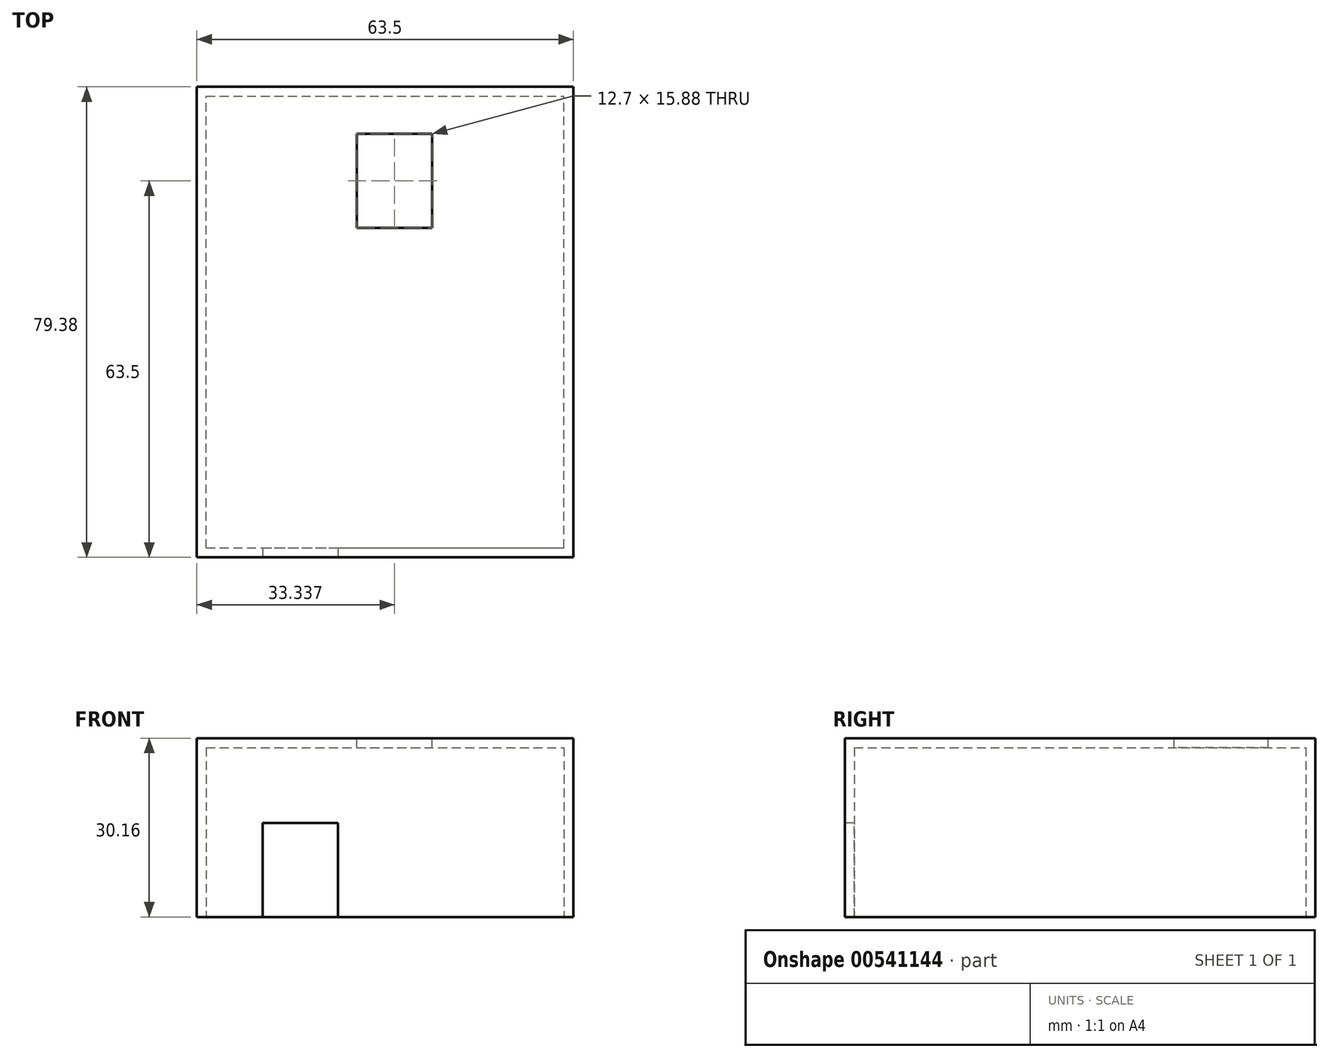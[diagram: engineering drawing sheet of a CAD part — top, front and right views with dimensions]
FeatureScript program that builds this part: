
annotation { "Feature Type Name" : "Feature", "Feature Type Description" : "" }
export const myFeature = defineFeature(function(context is Context, id is Id, definition is map)
    precondition{}
    {
        {
            var Q0;
            Q0=qCreatedBy(makeId("Top.planeOp"),FACE);
            var sketch = newSketch(context, id + "F0", { "sketchPlane" : qUnion([Q0])});
            skLineSegment(sketch, "E0.bottom", {"start": v(0, 0) * mm, "end": v(63.5, 0) * mm});
            skLineSegment(sketch, "E0.top", {"start": v(0, 79.38) * mm, "end": v(63.5, 79.38) * mm});
            skLineSegment(sketch, "E0.left", {"start": v(0, 0) * mm, "end": v(0, 79.38) * mm});
            skLineSegment(sketch, "E0.right", {"start": v(63.5, 0) * mm, "end": v(63.5, 79.38) * mm});
            skLineSegment(sketch, "E1.0", {"start": v(1.59, 77.79) * mm, "end": v(61.91, 77.79) * mm});
            skLineSegment(sketch, "E2.0", {"start": v(1.59, 1.59) * mm, "end": v(1.59, 77.79) * mm});
            skLineSegment(sketch, "E3.0", {"start": v(61.91, 1.59) * mm, "end": v(61.91, 77.79) * mm});
            skLineSegment(sketch, "E4.0", {"start": v(1.59, 1.59) * mm, "end": v(61.91, 1.59) * mm});
            skSolve(sketch);
        }
        {
            var Q0;
            Q0=makeQuery(id+"F0.imprint","IMPRINT",FACE,{"disambiguationData":[TD([[makeQuery(id+"F0.imprint","IMPRINT",EDGE,{"derivedFrom":sQuery(id+"F0.wireOp",EDGE,"E0.bottom")}),1.0]])]});
            extrude(context, id + "F1", {"entities" : qUnion([Q0]), "depth" : 30.16 * mm, "offsetDistance" : 25.4 * mm});
        }
        {
            var Q0;
            Q0=makeQuery(id+"F1.opExtrude","SWEPT_FACE",FACE,{"disambiguationData":[OSD([sQuery(id+"F0.wireOp",EDGE,"E1.0")])]});
            var sketch = newSketch(context, id + "F2", { "sketchPlane" : qUnion([Q0])});
            skLineSegment(sketch, "E5.bottom", {"start": v(1.59, 30.16) * mm, "end": v(61.91, 30.16) * mm});
            skLineSegment(sketch, "E5.top", {"start": v(1.59, 28.58) * mm, "end": v(61.91, 28.58) * mm});
            skLineSegment(sketch, "E5.left", {"start": v(1.59, 30.16) * mm, "end": v(1.59, 28.58) * mm});
            skLineSegment(sketch, "E5.right", {"start": v(61.91, 30.16) * mm, "end": v(61.91, 28.58) * mm});
            skSolve(sketch);
        }
        {
            var Q0;
            Q0 = qSketchRegion(id + "F2", true);
            extrude(context, id + "F3", {"entities" : qUnion([Q0]), "operationType" : NewBodyOperationType.ADD, "depth" : 76.2 * mm, "offsetDistance" : 25.4 * mm});
        }
        {
            var Q0;
            Q0=makeQuery(id+"F3.boolean.opBoolean","MERGE",FACE,{"derivedFrom":[makeQuery(id+"F1.opExtrude","CAP_FACE",FACE,{"disambiguationData":[OSD([sQuery(id+"F0.wireOp",EDGE,"E0.bottom"),sQuery(id+"F0.wireOp",EDGE,"E0.top"),sQuery(id+"F0.wireOp",EDGE,"E0.left"),sQuery(id+"F0.wireOp",EDGE,"E0.right"),sQuery(id+"F0.wireOp",EDGE,"E1.0"),sQuery(id+"F0.wireOp",EDGE,"E2.0"),sQuery(id+"F0.wireOp",EDGE,"E3.0"),sQuery(id+"F0.wireOp",EDGE,"E4.0")])],"isStart":false}),makeQuery(id+"F3.opExtrude","SWEPT_FACE",FACE,{"disambiguationData":[OSD([sQuery(id+"F2.wireOp",EDGE,"E5.bottom")])]})]});
            var sketch = newSketch(context, id + "F4", { "sketchPlane" : qUnion([Q0])});
            skLineSegment(sketch, "E6.bottom", {"start": v(26.99, 71.44) * mm, "end": v(39.69, 71.44) * mm});
            skLineSegment(sketch, "E6.top", {"start": v(26.99, 55.56) * mm, "end": v(39.69, 55.56) * mm});
            skLineSegment(sketch, "E6.left", {"start": v(26.99, 71.44) * mm, "end": v(26.99, 55.56) * mm});
            skLineSegment(sketch, "E6.right", {"start": v(39.69, 71.44) * mm, "end": v(39.69, 55.56) * mm});
            skSolve(sketch);
        }
        {
            var Q0;
            Q0 = qSketchRegion(id + "F4", true);
            extrude(context, id + "F5", {"entities" : qUnion([Q0]), "operationType" : NewBodyOperationType.REMOVE, "oppositeDirection" : true, "depth" : 1.59 * mm, "offsetDistance" : 25.4 * mm});
        }
        {
            var Q0;
            Q0=makeQuery(id+"F1.opExtrude","SWEPT_FACE",FACE,{"disambiguationData":[OSD([sQuery(id+"F0.wireOp",EDGE,"E0.bottom")])]});
            var sketch = newSketch(context, id + "F6", { "sketchPlane" : qUnion([Q0])});
            skLineSegment(sketch, "E7.bottom", {"start": v(11.11, 0) * mm, "end": v(23.81, 0) * mm});
            skLineSegment(sketch, "E7.top", {"start": v(11.11, 15.88) * mm, "end": v(23.81, 15.88) * mm});
            skLineSegment(sketch, "E7.left", {"start": v(11.11, 0) * mm, "end": v(11.11, 15.88) * mm});
            skLineSegment(sketch, "E7.right", {"start": v(23.81, 0) * mm, "end": v(23.81, 15.88) * mm});
            skSolve(sketch);
        }
        {
            var Q0;
            Q0 = qSketchRegion(id + "F6", true);
            extrude(context, id + "F7", {"entities" : qUnion([Q0]), "operationType" : NewBodyOperationType.REMOVE, "oppositeDirection" : true, "depth" : 1.59 * mm, "offsetDistance" : 25.4 * mm});
        }
    });
